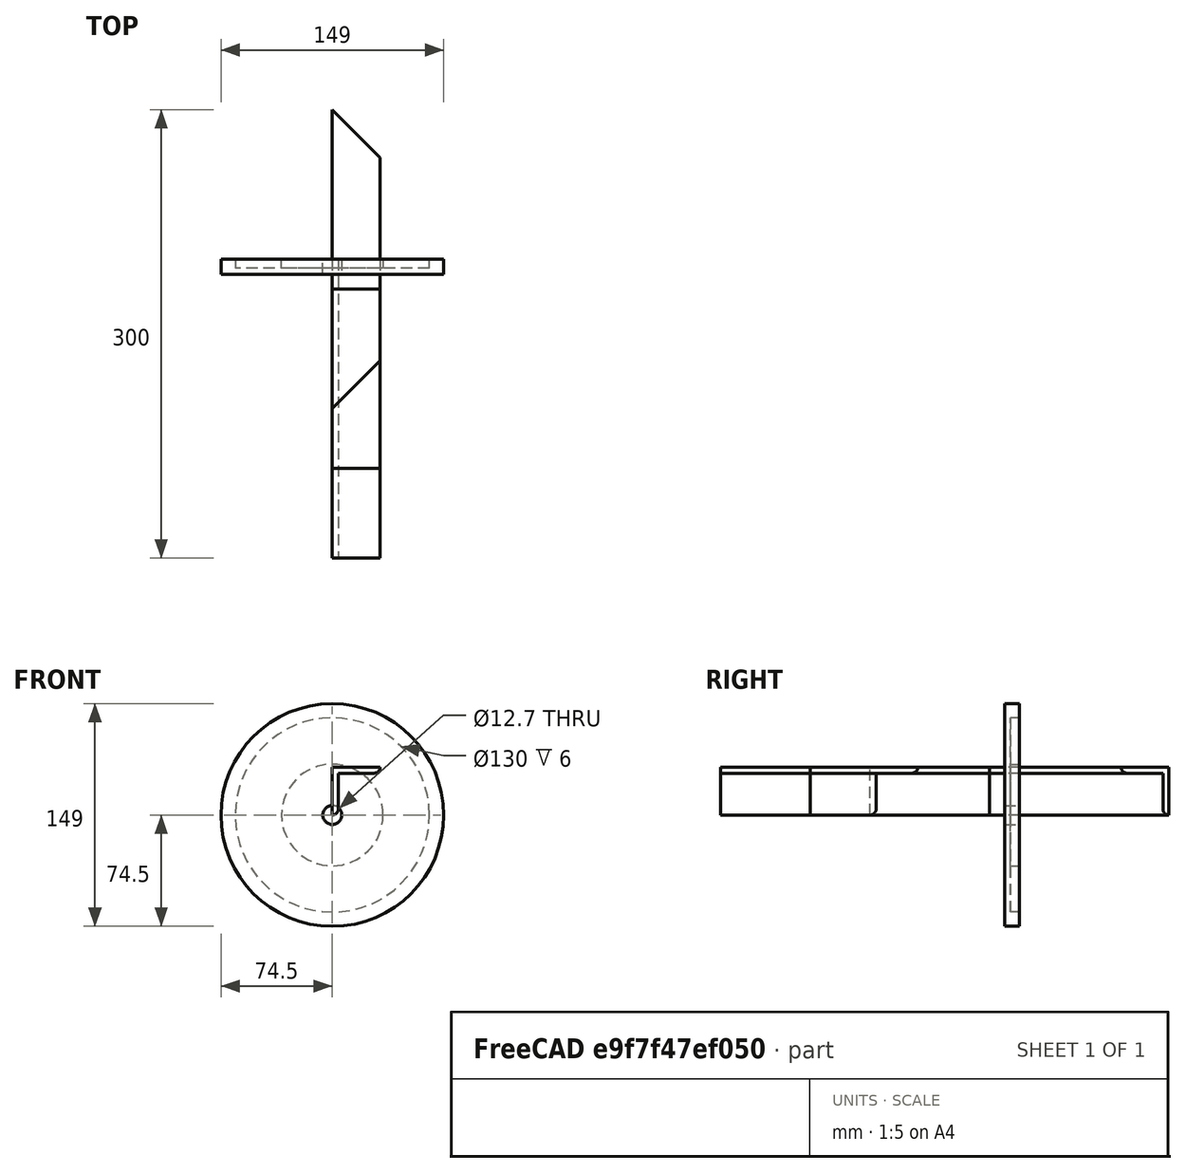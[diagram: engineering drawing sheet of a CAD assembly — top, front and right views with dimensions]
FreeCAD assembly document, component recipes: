
FREECAD ASSEMBLY — COMPONENT RECIPES ("sharpener")

This assembly document has 12 components, labeled P0..P11 below (a component is one placed body or linked part). 5 of them carry a construction recipe — the FreeCAD feature program that regenerates the part from scratch, quoted from this document or its linked companion documents; the rest are supplied as boundary geometry only. No exploded tour is included for this assembly.
COMPONENT P0 — recipe-attached ("corner_200", modeled in this document).
Construction recipe (the document's own serialized feature program — sketch geometry with constraints, then the solid features built on it; lengths are millimeters unless a unit is written):

FEATURE [Sketcher::SketchObject] Sketch024
  FullyConstrained = true
  MapMode = 5
  Placement = pos=(0,0,0) rot=(1,0,0;1.5708rad)
  Support = -> [XZ_Plane019]
  sketch-geometry (6):
    g0: LineSegment StartX=-7e-16 StartY=0 StartZ=0 EndX=0 EndY=32 EndZ=0
    g1: LineSegment StartX=0 StartY=32 StartZ=0 EndX=32 EndY=32 EndZ=0
    g2: LineSegment StartX=4 StartY=4 StartZ=0 EndX=4 EndY=28 EndZ=0
    g3: LineSegment StartX=4 StartY=28 StartZ=0 EndX=28 EndY=28 EndZ=0
    g4: ArcOfCircle CenterX=28 CenterY=32 CenterZ=0 NormalX=0 NormalY=0 NormalZ=1 AngleXU=0 Radius=4 StartAngle=4.71239 EndAngle=6.28319
    g5: ArcOfCircle CenterX=0 CenterY=4 CenterZ=0 NormalX=0 NormalY=0 NormalZ=1 AngleXU=0 Radius=4 StartAngle=4.71239 EndAngle=6.28319
  constraints (19):
    c: Coincident(g0,g-1)
    c: PointOnObject(g0,g-2)
    c: Coincident(g1,g0)
    c: Horizontal(g1)
    c: Vertical(g2)
    c: Coincident(g3,g2)
    c: Horizontal(g3)
    c: DistanceX(g0,g2) = 4
    c: DistanceY(g3,g1) = 4
    c: DistanceX(g0,g1) = 32
    c: DistanceY(g0,g0) = 32
    c: DistanceX(g2,g3) = 24
    c: DistanceY(g2,g2) = 24
    c: PointOnObject(g4,g1)
    c: Coincident(g4,g3)
    c: Coincident(g4,g1)
    c: PointOnObject(g5,g0)
    c: Coincident(g5,g2)
    c: Coincident(g5,g0)
FEATURE [PartDesign::Pad] Pad019
  Direction = (1,1,1)
  Length = 200
  Length2 = 100
  Placement = pos=(0,0,0) rot=(1,0,0;1.5708rad)
  Profile = -> Sketch024
  Type = 0
FEATURE [PartDesign::CoordinateSystem] LCS_14
  AttacherType = Attacher::AttachEngine3D
  MapMode = 7
  Placement = pos=(-7e-16,-200,4.44e-14) rot=(0,1,0;3.14159rad)
  Support = -> [Pad019]
FEATURE [PartDesign::CoordinateSystem] LCS_20
  AttacherType = Attacher::AttachEngine3D
  MapMode = 7
  Placement = pos=(0,-200,32) rot=(0.57735,-0.57735,-0.57735;2.0944rad)
  Support = -> [Pad019]
FEATURE [PartDesign::CoordinateSystem] LCS_21
  AttacherType = Attacher::AttachEngine3D
  MapMode = 7
  Placement = pos=(0,7.1e-15,32) rot=(0.57735,-0.57735,-0.57735;2.0944rad)
  Support = -> [Pad019]
FEATURE [PartDesign::CoordinateSystem] LCS_22
  AttacherType = Attacher::AttachEngine3D
  MapMode = 7
  Placement = pos=(32,7.1e-15,32) rot=(0,0.707107,0.707107;3.14159rad)
  Support = -> [Pad019]
FEATURE [PartDesign::CoordinateSystem] LCS_23
  AttacherType = Attacher::AttachEngine3D
  MapMode = 7
  Placement = pos=(-7e-16,0,0) rot=(0,1,0;3.14159rad)
  Support = -> [Pad019]
FEATURE [PartDesign::CoordinateSystem] LCS_24
  AttacherType = Attacher::AttachEngine3D
  AttachmentOffset = pos=(0,0,-32) rot=(0,0,1;0rad)
  MapMode = 7
  Placement = pos=(32,-200,32) rot=(0.57735,-0.57735,-0.57735;2.0944rad)
  Support = -> [Pad019]
FEATURE [PartDesign::Body] Body008  label="corner_200"
  Group = -> [Sketch024,Pad019,LCS_14,LCS_20,LCS_21,LCS_22,LCS_23,LCS_24]
  Origin = -> Origin019
  Tip = -> Pad019
COMPONENT P1 — recipe-attached ("corner", modeled in this document).
Construction recipe (the document's own serialized feature program — sketch geometry with constraints, then the solid features built on it; lengths are millimeters unless a unit is written):

FEATURE [Sketcher::SketchObject] Sketch025
  FullyConstrained = true
  MapMode = 5
  Placement = pos=(0,0,0) rot=(1,0,0;1.5708rad)
  Support = -> [XZ_Plane020]
  sketch-geometry (6):
    g0: LineSegment StartX=-7e-16 StartY=0 StartZ=0 EndX=0 EndY=32 EndZ=0
    g1: LineSegment StartX=0 StartY=32 StartZ=0 EndX=32 EndY=32 EndZ=0
    g2: LineSegment StartX=4 StartY=4 StartZ=0 EndX=4 EndY=28 EndZ=0
    g3: LineSegment StartX=4 StartY=28 StartZ=0 EndX=28 EndY=28 EndZ=0
    g4: ArcOfCircle CenterX=28 CenterY=32 CenterZ=0 NormalX=0 NormalY=0 NormalZ=1 AngleXU=0 Radius=4 StartAngle=4.71239 EndAngle=6.28319
    g5: ArcOfCircle CenterX=0 CenterY=4 CenterZ=0 NormalX=0 NormalY=0 NormalZ=1 AngleXU=0 Radius=4 StartAngle=4.71239 EndAngle=6.28319
  constraints (19):
    c: Coincident(g0,g-1)
    c: PointOnObject(g0,g-2)
    c: Coincident(g1,g0)
    c: Horizontal(g1)
    c: Vertical(g2)
    c: Coincident(g3,g2)
    c: Horizontal(g3)
    c: DistanceX(g0,g2) = 4
    c: DistanceY(g3,g1) = 4
    c: DistanceX(g0,g1) = 32
    c: DistanceY(g0,g0) = 32
    c: DistanceX(g2,g3) = 24
    c: DistanceY(g2,g2) = 24
    c: PointOnObject(g4,g1)
    c: Coincident(g4,g3)
    c: Coincident(g4,g1)
    c: PointOnObject(g5,g0)
    c: Coincident(g5,g2)
    c: Coincident(g5,g0)
FEATURE [PartDesign::Pad] Pad020
  Direction = (1,1,1)
  Length = 140
  Length2 = 100
  Placement = pos=(0,0,0) rot=(1,0,0;1.5708rad)
  Profile = -> Sketch025
  Type = 0
FEATURE [PartDesign::CoordinateSystem] LCS_13
  AttacherType = Attacher::AttachEngine3D
  MapMode = 7
  Placement = pos=(-7e-16,-140,3.11e-14) rot=(0,1,0;3.14159rad)
  Support = -> [Pad020]
FEATURE [PartDesign::CoordinateSystem] LCS_15
  AttacherType = Attacher::AttachEngine3D
  MapMode = 7
  Placement = pos=(-7e-16,0,0) rot=(0,1,0;3.14159rad)
  Support = -> [Pad020]
FEATURE [PartDesign::CoordinateSystem] LCS_16
  AttacherType = Attacher::AttachEngine3D
  MapMode = 7
  Placement = pos=(0,-140,32) rot=(0.57735,-0.57735,-0.57735;2.0944rad)
  Support = -> [Pad020]
FEATURE [PartDesign::CoordinateSystem] LCS_17
  AttacherType = Attacher::AttachEngine3D
  MapMode = 7
  Placement = pos=(0,7.1e-15,32) rot=(0.57735,-0.57735,-0.57735;2.0944rad)
  Support = -> [Pad020]
FEATURE [PartDesign::CoordinateSystem] LCS_18
  AttacherType = Attacher::AttachEngine3D
  MapMode = 7
  Placement = pos=(32,7.1e-15,32) rot=(0,0.707107,0.707107;3.14159rad)
  Support = -> [Pad020]
FEATURE [PartDesign::CoordinateSystem] LCS_19
  AttacherType = Attacher::AttachEngine3D
  AttachmentOffset = pos=(0,0,-32) rot=(0,0,1;0rad)
  MapMode = 7
  Placement = pos=(32,-140,32) rot=(0.57735,-0.57735,-0.57735;2.0944rad)
  Support = -> [Pad020]
FEATURE [PartDesign::CoordinateSystem] LCS_25  label="LCS_inner_corner"
  AttacherType = Attacher::AttachEngine3D
  AttachmentOffset = pos=(0,38,-32) rot=(0,0,1;0rad)
  MapMode = 5
  Placement = pos=(0,-38,7.1e-15) rot=(0,0,1;3.14159rad)
  Support = -> [Pad020]
FEATURE [PartDesign::CoordinateSystem] LCS_inner_corner1
  AttacherType = Attacher::AttachEngine3D
  AttachmentOffset = pos=(0,0,-102) rot=(0,0,1;0rad)
  MapMode = 7
  Placement = pos=(-1e-15,-102,2.26e-14) rot=(0,0.707107,0.707107;3.14159rad)
  Support = -> [Pad020]
FEATURE [PartDesign::Body] Body009  label="corner"
  Group = -> [Sketch025,Pad020,LCS_13,LCS_15,LCS_16,LCS_17,LCS_18,LCS_19,LCS_25,LCS_inner_corner1]
  Origin = -> Origin020
  Tip = -> Pad020
COMPONENT P2 — recipe-attached ("corner_204", modeled in this document).
Construction recipe (the document's own serialized feature program — sketch geometry with constraints, then the solid features built on it; lengths are millimeters unless a unit is written):

FEATURE [Sketcher::SketchObject] Sketch026
  FullyConstrained = true
  MapMode = 5
  Placement = pos=(0,0,0) rot=(1,0,0;1.5708rad)
  Support = -> [XZ_Plane021]
  sketch-geometry (6):
    g0: LineSegment StartX=-7e-16 StartY=0 StartZ=0 EndX=0 EndY=32 EndZ=0
    g1: LineSegment StartX=0 StartY=32 StartZ=0 EndX=32 EndY=32 EndZ=0
    g2: LineSegment StartX=4 StartY=4 StartZ=0 EndX=4 EndY=28 EndZ=0
    g3: LineSegment StartX=4 StartY=28 StartZ=0 EndX=28 EndY=28 EndZ=0
    g4: ArcOfCircle CenterX=28 CenterY=32 CenterZ=0 NormalX=0 NormalY=0 NormalZ=1 AngleXU=0 Radius=4 StartAngle=4.71239 EndAngle=6.28319
    g5: ArcOfCircle CenterX=0 CenterY=4 CenterZ=0 NormalX=0 NormalY=0 NormalZ=1 AngleXU=0 Radius=4 StartAngle=4.71239 EndAngle=6.28319
  constraints (19):
    c: Coincident(g0,g-1)
    c: PointOnObject(g0,g-2)
    c: Coincident(g1,g0)
    c: Horizontal(g1)
    c: Vertical(g2)
    c: Coincident(g3,g2)
    c: Horizontal(g3)
    c: DistanceX(g0,g2) = 4
    c: DistanceY(g3,g1) = 4
    c: DistanceX(g0,g1) = 32
    c: DistanceY(g0,g0) = 32
    c: DistanceX(g2,g3) = 24
    c: DistanceY(g2,g2) = 24
    c: PointOnObject(g4,g1)
    c: Coincident(g4,g3)
    c: Coincident(g4,g1)
    c: PointOnObject(g5,g0)
    c: Coincident(g5,g2)
    c: Coincident(g5,g0)
FEATURE [PartDesign::Pad] Pad021
  Direction = (1,1,1)
  Length = 20
  Length2 = 100
  Placement = pos=(0,0,0) rot=(1,0,0;1.5708rad)
  Profile = -> Sketch026
  Type = 0
FEATURE [PartDesign::CoordinateSystem] LCS_26
  AttacherType = Attacher::AttachEngine3D
  AttachmentOffset = pos=(0,0,-10) rot=(0,0,1;0rad)
  MapMode = 7
  Placement = pos=(0,-10,32) rot=(0,0.707107,0.707107;3.14159rad)
  Support = -> [Pad021]
FEATURE [PartDesign::Body] Body010  label="corner_204"
  Group = -> [Sketch026,Pad021,LCS_26]
  Origin = -> Origin021
  Tip = -> Pad021
COMPONENT P3 — recipe-attached ("corner_200005", modeled in this document).
Construction recipe (the document's own serialized feature program — sketch geometry with constraints, then the solid features built on it; lengths are millimeters unless a unit is written):

FEATURE [Sketcher::SketchObject] Sketch027
  FullyConstrained = true
  MapMode = 5
  Placement = pos=(0,0,0) rot=(1,0,0;1.5708rad)
  Support = -> [XZ_Plane022]
  sketch-geometry (6):
    g0: LineSegment StartX=-7e-16 StartY=0 StartZ=0 EndX=0 EndY=32 EndZ=0
    g1: LineSegment StartX=0 StartY=32 StartZ=0 EndX=32 EndY=32 EndZ=0
    g2: LineSegment StartX=4 StartY=4 StartZ=0 EndX=4 EndY=28 EndZ=0
    g3: LineSegment StartX=4 StartY=28 StartZ=0 EndX=28 EndY=28 EndZ=0
    g4: ArcOfCircle CenterX=28 CenterY=32 CenterZ=0 NormalX=0 NormalY=0 NormalZ=1 AngleXU=0 Radius=4 StartAngle=4.71239 EndAngle=6.28319
    g5: ArcOfCircle CenterX=0 CenterY=4 CenterZ=0 NormalX=0 NormalY=0 NormalZ=1 AngleXU=0 Radius=4 StartAngle=4.71239 EndAngle=6.28319
  constraints (19):
    c: Coincident(g0,g-1)
    c: PointOnObject(g0,g-2)
    c: Coincident(g1,g0)
    c: Horizontal(g1)
    c: Vertical(g2)
    c: Coincident(g3,g2)
    c: Horizontal(g3)
    c: DistanceX(g0,g2) = 4
    c: DistanceY(g3,g1) = 4
    c: DistanceX(g0,g1) = 32
    c: DistanceY(g0,g0) = 32
    c: DistanceX(g2,g3) = 24
    c: DistanceY(g2,g2) = 24
    c: PointOnObject(g4,g1)
    c: Coincident(g4,g3)
    c: Coincident(g4,g1)
    c: PointOnObject(g5,g0)
    c: Coincident(g5,g2)
    c: Coincident(g5,g0)
FEATURE [PartDesign::Pad] Pad022
  Direction = (1,1,1)
  Length = 200
  Length2 = 100
  Midplane = true
  Placement = pos=(0,0,0) rot=(1,0,0;1.5708rad)
  Profile = -> Sketch027
  Type = 0
FEATURE [Sketcher::SketchObject] Sketch028
  ExternalGeometry = -> [Pad022]
  FullyConstrained = true
  MapMode = 5
  Placement = pos=(0,7.1e-15,32) rot=(0,0,1;3.14159rad)
  Support = -> [Pad022]
  sketch-geometry (6):
    g0: LineSegment StartX=0 StartY=100 StartZ=0 EndX=-32 EndY=100 EndZ=0
    g1: LineSegment StartX=-32 StartY=68 StartZ=0 EndX=-32 EndY=100 EndZ=0
    g2: LineSegment StartX=-32 StartY=68 StartZ=0 EndX=0 EndY=100 EndZ=0
    g3: LineSegment StartX=0 StartY=-100 StartZ=0 EndX=-32 EndY=-100 EndZ=0
    g4: LineSegment StartX=-32 StartY=-100 StartZ=0 EndX=-32 EndY=-68 EndZ=0
    g5: LineSegment StartX=0 StartY=-100 StartZ=0 EndX=-32 EndY=-68 EndZ=0
  constraints (14):
    c: Coincident(g0,g-3)
    c: Coincident(g0,g-3)
    c: Coincident(g1,g0)
    c: Vertical(g1)
    c: Coincident(g2,g1)
    c: Coincident(g2,g0)
    c: DistanceY(g2,g0) = 32
    c: Coincident(g3,g-4)
    c: Coincident(g3,g-4)
    c: Coincident(g4,g3)
    c: Vertical(g4)
    c: Coincident(g5,g3)
    c: Coincident(g5,g4)
    c: DistanceY(g3,g4) = 32
FEATURE [PartDesign::Pocket] Pocket005
  BaseFeature = -> Pad022
  Length = 32
  Length2 = 100
  Placement = pos=(0,0,0) rot=(1,0,0;1.5708rad)
  Profile = -> Sketch028
  Type = 0
FEATURE [PartDesign::CoordinateSystem] LCS_27
  AttacherType = Attacher::AttachEngine3D
  MapMode = 45
  Placement = pos=(-4e-16,-100,16) rot=(0,0,1;0rad)
  Support = -> [Pocket005]
FEATURE [PartDesign::CoordinateSystem] LCS_28
  AttacherType = Attacher::AttachEngine3D
  MapMode = 45
  Placement = pos=(-4e-16,100,16) rot=(0,0,1;0rad)
  Support = -> [Pocket005]
FEATURE [PartDesign::Body] Body011  label="corner_200005"
  Group = -> [Sketch027,Pad022,Sketch028,Pocket005,LCS_27,LCS_28]
  Origin = -> Origin022
  Tip = -> Pocket005
COMPONENT P4 — geometry summary ("right_bracket"; no construction recipe available for this part):
  bounding box: 150.0 x 150.0 x 32.0 mm
  tessellated surface: 788 triangles
  volume: 65536 mm^3 (9% of its bounding box)
COMPONENT P5 — geometry summary ("left_bracket"; no construction recipe available for this part):
  bounding box: 150.0 x 150.0 x 32.0 mm
  tessellated surface: 1,008 triangles
  volume: 100506 mm^3 (14% of its bounding box)
COMPONENT P6 — geometry summary ("adapter"; no construction recipe available for this part):
  bounding box: 55.0 x 19.0 x 19.0 mm
  tessellated surface: 1,404 triangles
  volume: 10166 mm^3 (51% of its bounding box)
  symmetry: revolution-symmetric about the y axis through its bounding-box center; mirror-symmetric across its x mid-plane, z mid-plane
COMPONENT P7 — recipe-attached ("platform", modeled in this document).
Construction recipe (the document's own serialized feature program — sketch geometry with constraints, then the solid features built on it; lengths are millimeters unless a unit is written):

FEATURE [Sketcher::SketchObject] Sketch016
  FullyConstrained = true
  MapMode = 5
  Placement = pos=(0,0,0) rot=(1,0,0;1.5708rad)
  Support = -> [XZ_Plane014]
  sketch-geometry (1):
    g0: Circle CenterX=0 CenterY=0 CenterZ=0 NormalX=0 NormalY=0 NormalZ=1 AngleXU=0 Radius=34
  constraints (2):
    c: Coincident(g0,g-1)
    c: Diameter(g0) = 68
FEATURE [PartDesign::Pad] Pad013
  Direction = (1,1,1)
  Length = 6
  Length2 = 100
  Placement = pos=(0,0,0) rot=(1,0,0;1.5708rad)
  Profile = -> Sketch016
  Type = 0
FEATURE [Sketcher::SketchObject] Sketch017
  FullyConstrained = true
  MapMode = 5
  Placement = pos=(0,-6,1.3e-15) rot=(1,0,0;1.5708rad)
  Support = -> [Pad013]
  sketch-geometry (1):
    g0: Circle CenterX=0 CenterY=0 CenterZ=0 NormalX=0 NormalY=0 NormalZ=1 AngleXU=0 Radius=74.5
  constraints (2):
    c: Coincident(g0,g-1)
    c: Diameter(g0) = 149
FEATURE [PartDesign::Pad] Pad014
  BaseFeature = -> Pad013
  Direction = (1,1,1)
  Length = 4
  Length2 = 100
  Placement = pos=(0,0,0) rot=(1,0,0;1.5708rad)
  Profile = -> Sketch017
  Type = 0
FEATURE [Sketcher::SketchObject] Sketch018
  FullyConstrained = true
  MapMode = 5
  Placement = pos=(0,-6,4.6e-15) rot=(-1,0,0;1.5708rad)
  Support = -> [Pad014]
  sketch-geometry (2):
    g0: Circle CenterX=0 CenterY=0 CenterZ=0 NormalX=0 NormalY=0 NormalZ=1 AngleXU=0 Radius=65
    g1: Circle CenterX=0 CenterY=0 CenterZ=0 NormalX=0 NormalY=0 NormalZ=1 AngleXU=0 Radius=74.5
  constraints (4):
    c: Coincident(g0,g-1)
    c: Coincident(g1,g0)
    c: Diameter(g1) = 149
    c: Diameter(g0) = 130
FEATURE [PartDesign::Pad] Pad015
  BaseFeature = -> Pad014
  Direction = (1,1,1)
  Length = 6
  Length2 = 100
  Placement = pos=(0,0,0) rot=(1,0,0;1.5708rad)
  Profile = -> Sketch018
  Type = 0
FEATURE [Sketcher::SketchObject] Sketch019
  FullyConstrained = true
  MapMode = 5
  Placement = pos=(0,0,0) rot=(-1,0,0;1.5708rad)
  Support = -> [Pad015]
  sketch-geometry (1):
    g0: Circle CenterX=0 CenterY=0 CenterZ=0 NormalX=0 NormalY=0 NormalZ=1 AngleXU=0 Radius=6.35
  constraints (2):
    c: Coincident(g0,g-1)
    c: Diameter(g0) = 12.7
FEATURE [PartDesign::Pocket] Pocket003
  BaseFeature = -> Pad015
  Length = 5
  Length2 = 100
  Placement = pos=(0,0,0) rot=(1,0,0;1.5708rad)
  Profile = -> Sketch019
  Type = 1
FEATURE [PartDesign::Body] Body005
  Group = -> [Sketch016,Pad013,Sketch017,Pad014,Sketch018,Pad015,Sketch019,Pocket003]
  Origin = -> Origin014
  Tip = -> Pocket003
COMPONENT P8 — geometry summary ("disc"; no construction recipe available for this part):
  bounding box: 152.0 x 152.0 x 1.0 mm
  tessellated surface: 1,008 triangles
  volume: 18019 mm^3 (78% of its bounding box)
  symmetry: 2-fold rotationally symmetric about the x axis; revolution-symmetric about the y axis through its bounding-box center; 2-fold rotationally symmetric about the z axis; mirror-symmetric across its x mid-plane, y mid-plane, z mid-plane
COMPONENT P9 — geometry summary ("nut"; no construction recipe available for this part):
  bounding box: 37.0 x 37.0 x 13.0 mm
  tessellated surface: 1,536 triangles
  volume: 4687 mm^3 (26% of its bounding box)
  symmetry: 6-fold rotationally symmetric about the y axis; mirror-symmetric across its x mid-plane, z mid-plane
COMPONENT P10 — geometry summary ("motor"; no construction recipe available for this part):
  bounding box: 140.0 x 85.0 x 85.0 mm
  tessellated surface: 26,760 triangles
  volume: 1001697 mm^3 (99% of its bounding box)
  symmetry: 2-fold rotationally symmetric about the y axis; mirror-symmetric across its x mid-plane, z mid-plane
COMPONENT P11 — geometry summary ("support"; no construction recipe available for this part):
  bounding box: 500.0 x 160.0 x 10.0 mm
  tessellated surface: 12 triangles
  volume: 800000 mm^3 (100% of its bounding box)
  symmetry: 2-fold rotationally symmetric about the x axis; 2-fold rotationally symmetric about the y axis; 2-fold rotationally symmetric about the z axis; mirror-symmetric across its x mid-plane, y mid-plane, z mid-plane
PROVENANCE & LICENSES
A FreeCAD (.FCStd) document from a public repository crawl; recipes are the document's own serialized feature recipes (and, for linked parts, companion documents' recipes).
License: as declared in the source repository (recorded in the dataset sidecar).
